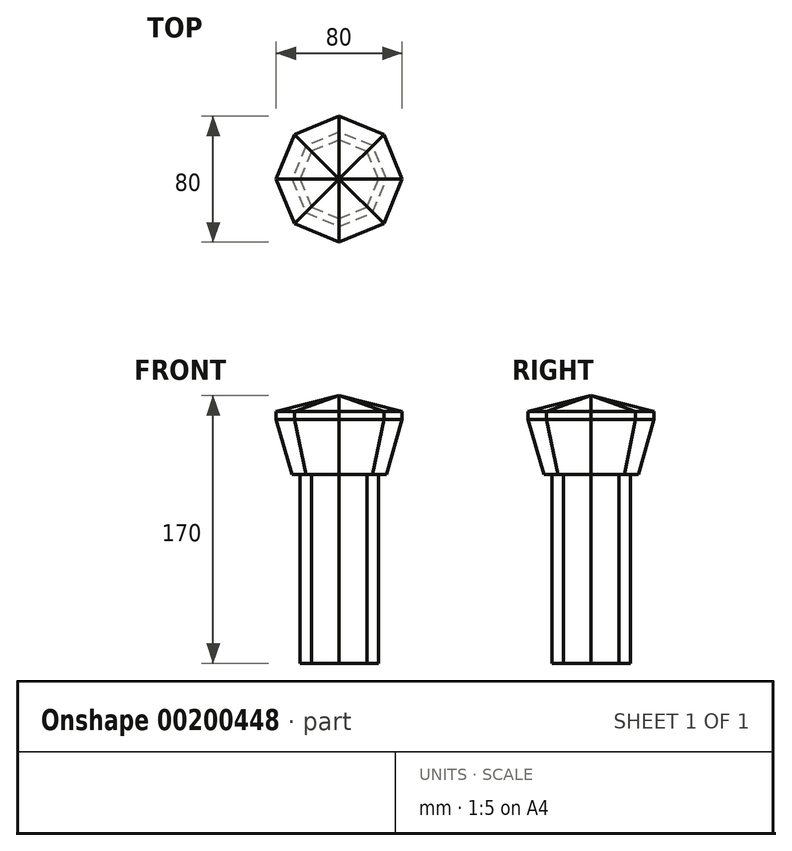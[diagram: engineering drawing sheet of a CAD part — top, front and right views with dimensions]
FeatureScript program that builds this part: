
annotation { "Feature Type Name" : "Feature", "Feature Type Description" : "" }
export const myFeature = defineFeature(function(context is Context, id is Id, definition is map)
    precondition{}
    {
        {
            var Q0;
            Q0=qCreatedBy(makeId("Front.planeOp"),FACE);
            var sketch = newSketch(context, id + "F0", { "sketchPlane" : qUnion([Q0])});
            skLineSegment(sketch, "E0", {"start": v(0, 170) * mm, "end": v(40, 160) * mm});
            skLineSegment(sketch, "E1", {"start": v(40, 160) * mm, "end": v(40, 155) * mm});
            skLineSegment(sketch, "E2", {"start": v(40, 155) * mm, "end": v(30, 120) * mm});
            skLineSegment(sketch, "E3", {"start": v(30, 120) * mm, "end": v(25, 120) * mm});
            skLineSegment(sketch, "E4", {"start": v(25, 120) * mm, "end": v(25, 0) * mm});
            skLineSegment(sketch, "E5", {"start": v(25, 0) * mm, "end": v(0, 0) * mm});
            skLineSegment(sketch, "E6", {"start": v(0, 0) * mm, "end": v(0, 170) * mm});
            skSolve(sketch);
        }
        {
            var Q0;
            Q0=sQuery(id+"F0.wireOp",EDGE,"E6");
            var Q1;
            Q1=qCreatedBy(makeId("Front.planeOp"),FACE);
            cPlane(context, id + "F1", {"entities" : qUnion([Q0, Q1]), "cplaneType" : CPlaneType.LINE_ANGLE, "offset" : 25.4 * mm, "angle" : 45 * degree, "width" : 152.4 * mm, "height" : 152.4 * mm});
        }
        {
            var Q0;
            Q0=qCreatedBy(id+"F1.planeOp",FACE);
            var sketch = newSketch(context, id + "F2", { "sketchPlane" : qUnion([Q0])});
            skLineSegment(sketch, "E7", {"start": v(0, 0) * mm, "end": v(0, 170) * mm});
            skLineSegment(sketch, "E8.MirrorCS", {"start": v(-40, 160) * mm, "end": v(-40, 155) * mm});
            skLineSegment(sketch, "E9.MirrorCS", {"start": v(-30, 120) * mm, "end": v(-25, 120) * mm});
            skLineSegment(sketch, "E10.MirrorCS", {"start": v(0, 170) * mm, "end": v(-40, 160) * mm});
            skLineSegment(sketch, "E11.MirrorCS", {"start": v(-40, 155) * mm, "end": v(-30, 120) * mm});
            skLineSegment(sketch, "E12.MirrorCS", {"start": v(-25, 120) * mm, "end": v(-25, 0) * mm});
            skLineSegment(sketch, "E13.MirrorCS", {"start": v(-25, 0) * mm, "end": v(0, 0) * mm});
            skSolve(sketch);
        }
        {
            var Q0;
            Q0=makeQuery(id+"F0.imprint","IMPRINT",FACE,{"disambiguationData":[TD([[makeQuery(id+"F0.imprint","IMPRINT",EDGE,{"derivedFrom":sQuery(id+"F0.wireOp",EDGE,"E0")}),-1.0]])]});
            var Q1;
            Q1=makeQuery(id+"F2.imprint","IMPRINT",FACE,{"disambiguationData":[TD([[makeQuery(id+"F2.imprint","IMPRINT",EDGE,{"derivedFrom":sQuery(id+"F2.wireOp",EDGE,"E7")}),1.0]])]});
            var Q2;
            Q2=sQuery(id+"F0.wireOp",VERTEX,"E4.end");
            var Q3;
            Q3=sQuery(id+"F2.wireOp",VERTEX,"E13.MirrorCS.start");
            loft(context, id + "F3", {"sheetProfilesArray" : [{ "sheetProfileEntities" : qUnion([Q0]) }, { "sheetProfileEntities" : qUnion([Q1]) }], "matchConnections" : true, "connections" : [{ "connectionEntities" : qUnion([Q2, Q3]), "connectionEdgeQueries" : qUnion([]), "connectionEdgeParameters" : [] }]});
        }
        {
            var Q0;
            Q0=makeQuery(id+"F3.opLoft","SWEPT_BODY",BODY,{"disambiguationData":[OSD([makeQuery(id+"F0.imprint","IMPRINT",FACE,{"disambiguationData":[TD([[makeQuery(id+"F0.imprint","IMPRINT",EDGE,{"derivedFrom":sQuery(id+"F0.wireOp",EDGE,"E0")}),-1.0]])]}),makeQuery(id+"F2.imprint","IMPRINT",FACE,{"disambiguationData":[TD([[makeQuery(id+"F2.imprint","IMPRINT",EDGE,{"derivedFrom":sQuery(id+"F2.wireOp",EDGE,"E7")}),1.0]])]})])]});
            var Q1;
            Q1=makeQuery(id+"F3.opLoft","CAP_EDGE",EDGE,{"disambiguationData":[OSD([sQuery(id+"F0.wireOp",EDGE,"E6"),sQuery(id+"F2.wireOp",EDGE,"E7")])],"isStart":false});
            circularPattern(context, id + "F4", {"entities" : qUnion([Q0]), "axis" : qUnion([Q1]), "angle" : 360 * degree, "instanceCount" : 8, "equalSpace" : true});
        }
    });
